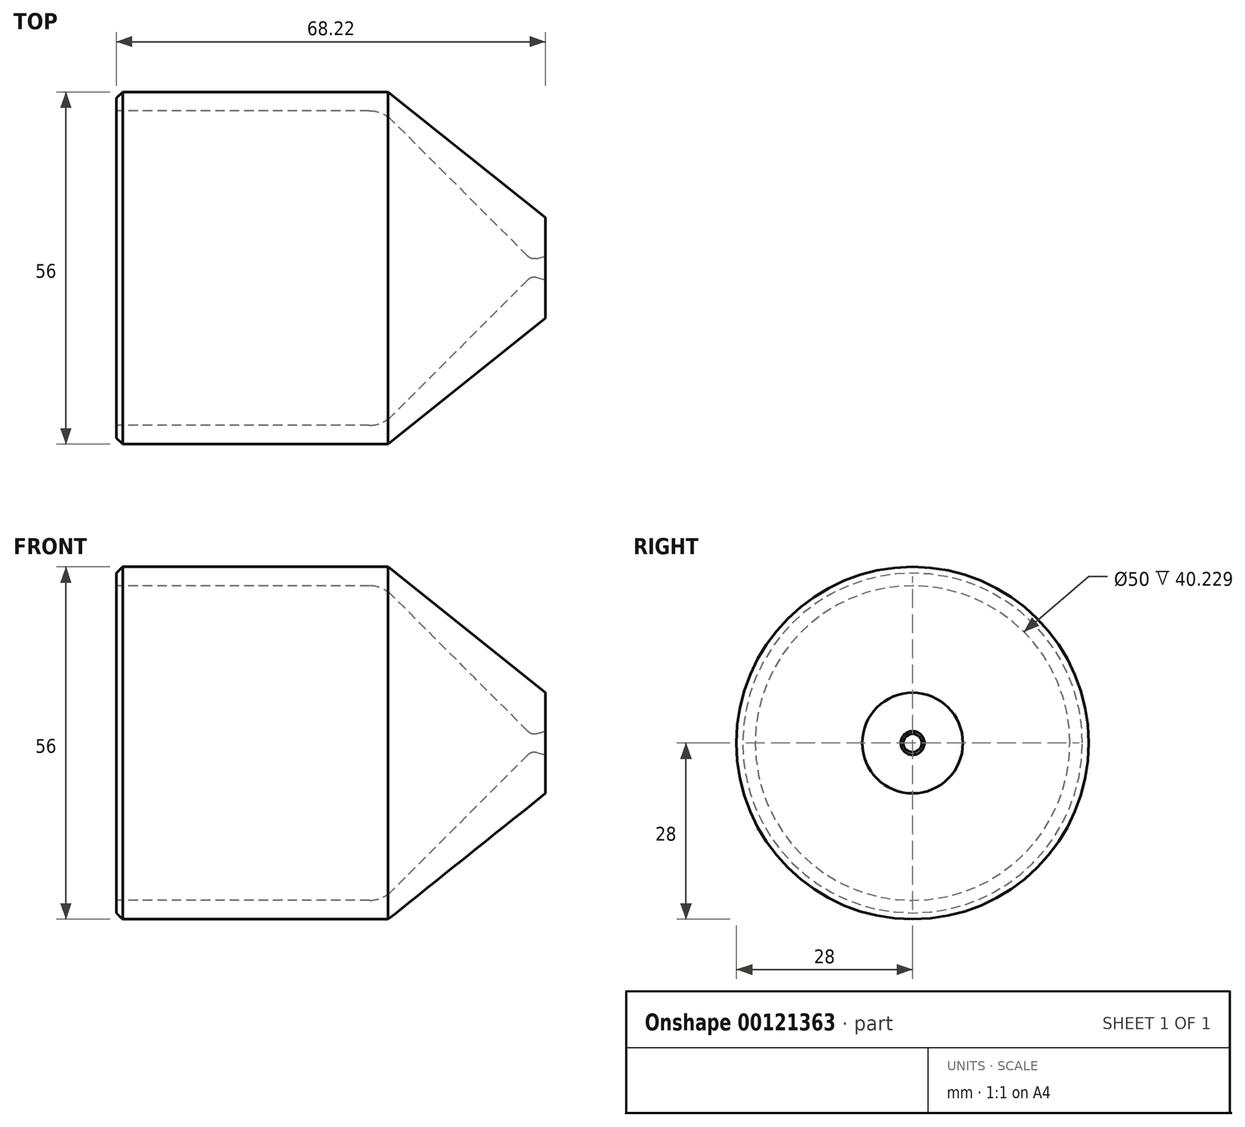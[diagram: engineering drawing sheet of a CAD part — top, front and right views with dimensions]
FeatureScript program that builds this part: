
annotation { "Feature Type Name" : "Feature", "Feature Type Description" : "" }
export const myFeature = defineFeature(function(context is Context, id is Id, definition is map)
    precondition{}
    {
        {
            var Q0;
            Q0=qCreatedBy(makeId("Front.planeOp"),FACE);
            var sketch = newSketch(context, id + "F0", { "sketchPlane" : qUnion([Q0])});
            skLineSegment(sketch, "E0", {"start": v(0, 1.46) * mm, "end": v(0, 2.92) * mm, "construction": true});
            skArc(sketch, "E1", {"start": v(0, 1.46) * mm, "mid": v(0.2, 1.47) * mm, "end": v(0.38, 1.5) * mm});
            skLineSegment(sketch, "E2", {"start": v(0, 2.92) * mm, "end": v(0.38, 1.5) * mm, "construction": true});
            skLineSegment(sketch, "E3", {"start": v(0, 0) * mm, "end": v(1.77, 0) * mm});
            skLineSegment(sketch, "E4", {"start": v(1.77, 0) * mm, "end": v(1.77, 1.88) * mm});
            skLineSegment(sketch, "E5", {"start": v(0.38, 1.5) * mm, "end": v(1.77, 1.88) * mm});
            skLineSegment(sketch, "E6", {"start": v(0, 0) * mm, "end": v(-66.45, 0) * mm});
            skLineSegment(sketch, "E7", {"start": v(-66.45, 0) * mm, "end": v(-66.45, 25) * mm});
            skLineSegment(sketch, "E8", {"start": v(-66.45, 25) * mm, "end": v(-26.22, 25) * mm});
            skArc(sketch, "E9", {"start": v(-1.03, 1.89) * mm, "mid": v(-0.56, 1.57) * mm, "end": v(0, 1.46) * mm});
            skLineSegment(sketch, "E10", {"start": v(0, 2.92) * mm, "end": v(-1.03, 1.89) * mm, "construction": true});
            skLineSegment(sketch, "E11", {"start": v(-1.03, 1.89) * mm, "end": v(-22.68, 23.54) * mm});
            skPoint(sketch, "E12.visualSharp", {"position": v(-24.14, 25) * mm});
            skArc(sketch, "E12.filletArc", {"start": v(-22.68, 23.54) * mm, "mid": v(-24.3, 24.62) * mm, "end": v(-26.22, 25) * mm});
            skSolve(sketch);
        }
        {
            var Q0;
            Q0=qCreatedBy(makeId("Front.planeOp"),FACE);
            var sketch = newSketch(context, id + "F1", { "sketchPlane" : qUnion([Q0])});
            skLineSegment(sketch, "E13.0", {"start": v(0, 0) * mm, "end": v(-66.45, 0) * mm});
            skLineSegment(sketch, "E13.1", {"start": v(-66.45, 0) * mm, "end": v(-66.45, 25) * mm});
            skLineSegment(sketch, "E13.2", {"start": v(-66.45, 25) * mm, "end": v(-26.22, 25) * mm});
            skLineSegment(sketch, "E13.3", {"start": v(0, 0) * mm, "end": v(1.77, 0) * mm});
            skLineSegment(sketch, "E14", {"start": v(-66.45, 25) * mm, "end": v(-66.45, 28) * mm});
            skLineSegment(sketch, "E15", {"start": v(-66.45, 28) * mm, "end": v(-26.22, 28) * mm});
            skLineSegment(sketch, "E16", {"start": v(-26.22, 28) * mm, "end": v(1.77, 28) * mm});
            skLineSegment(sketch, "E17", {"start": v(1.77, 0) * mm, "end": v(1.77, 28) * mm});
            skSolve(sketch);
        }
        {
            var Q0;
            Q0=makeQuery(id+"F0.imprint","IMPRINT",FACE,{"disambiguationData":[TD([[makeQuery(id+"F0.imprint","IMPRINT",EDGE,{"derivedFrom":sQuery(id+"F0.wireOp",EDGE,"E1")}),-1.0]])]});
            var Q1;
            Q1 = qSketchRegion(id + "F0", true);
            var Q2;
            Q2=sQuery(id+"F1.wireOp",EDGE,"E13.0");
            revolve(context, id + "F2", {"surfaceOperationType" : NewSurfaceOperationType.NEW, "entities" : qUnion([Q0, Q1]), "axis" : qUnion([Q2]), "revolveType" : RevolveType.FULL});
        }
        {
            var Q0;
            Q0=makeQuery(id+"F1.imprint","IMPRINT",FACE,{"disambiguationData":[TD([[makeQuery(id+"F1.imprint","IMPRINT",EDGE,{"derivedFrom":sQuery(id+"F1.wireOp",EDGE,"E13.0")}),-1.0]])]});
            var Q1;
            Q1=sQuery(id+"F1.wireOp",EDGE,"E13.0");
            revolve(context, id + "F3", {"entities" : qUnion([Q0]), "axis" : qUnion([Q1]), "revolveType" : RevolveType.FULL});
        }
        {
            var Q0;
            Q0 = qSketchRegion(id + "F0", true);
            var Q1;
            Q1=sQuery(id+"F0.wireOp",EDGE,"E6");
            revolve(context, id + "F4", {"operationType" : NewBodyOperationType.REMOVE, "entities" : qUnion([Q0]), "axis" : qUnion([Q1]), "revolveType" : RevolveType.FULL, "oppositeDirection" : true});
        }
        {
            var Q0;
            Q0=makeQuery(id+"F3.opRevolve","SWEPT_EDGE",EDGE,{"disambiguationData":[OSD([sQuery(id+"F1.wireOp",EDGE,"E16"),sQuery(id+"F1.wireOp",EDGE,"E17")])]});
            chamfer(context, id + "F5", {"entities" : qUnion([Q0]), "chamferType" : ChamferType.TWO_OFFSETS, "width1" : 20 * mm, "oppositeDirection" : false, "width2" : 25 * mm, "tangentPropagation" : true});
        }
        {
            var Q0;
            Q0=makeQuery(id+"F3.opRevolve","SWEPT_EDGE",EDGE,{"disambiguationData":[OSD([sQuery(id+"F1.wireOp",EDGE,"E14"),sQuery(id+"F1.wireOp",EDGE,"E15")])]});
            chamfer(context, id + "F6", {"entities" : qUnion([Q0]), "width" : 1 * mm, "tangentPropagation" : true});
        }
    });
